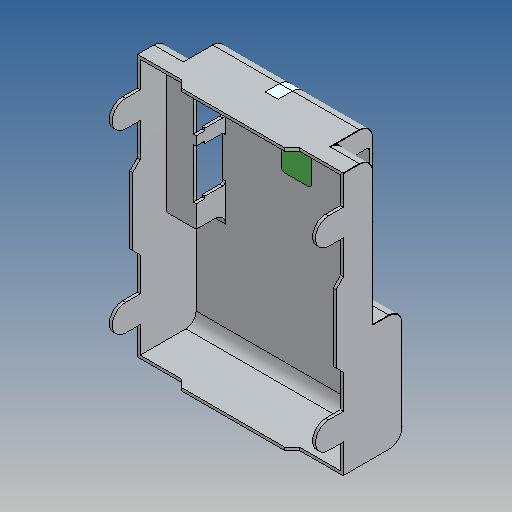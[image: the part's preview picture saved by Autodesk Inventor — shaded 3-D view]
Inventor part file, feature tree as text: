
AUTODESK INVENTOR PART (.ipt)
format: ipt  version: 2025 (Build 290162010, 162A)  size: 946,688 bytes
history: native  units: mm
features: sketch x4, extrude x3, fillet x2, direct_edit x1, delete_face x1, imported_body x1, revolve x1, move_body x1
ambient origin geometry x8: Origin, YZ Plane, XZ Plane, XY Plane, X Axis, Y Axis, Z Axis, Center Point
bodies: Volumenkörper1 (feature_tree), Volumenkörper2 (feature_tree), Volumenkörper3 (feature_tree)
feature tree (14):
  sketch  "Skizze1"  dims[d0=180.0deg d1=0.0mm d2=0.0mm d3=-0.58mm d4=10.0mm]
  direct_edit  "Direktbearbeitung1"
  delete_face  "Fläche löschen1"
  extrude  "Extrusion1"  TaperAngle=0.0deg  [1 undecoded]
  fillet  "Rundung2"  Radius=10.0mm
  extrude  "Extrusion2"  Depth=3.5mm TaperAngle=0.0deg
  extrude  "Extrusion3"  Depth=3.5mm TaperAngle=0.0deg
  fillet  "Rundung1"  Radius=0.1mm
  sketch  "Skizze2"  dims[d5=7.5mm d6=3.5mm d7=0.0mm]
  sketch  "Skizze3"  dims[d8=3.5mm d9=0.0mm d10=3.5mm d11=0.0mm d12=0.1mm]
  sketch  "Skizze4"  dims[d13=0.1mm]
  imported_body  "Basis1"
  revolve  "Drehen1"  [1 undecoded]
  move_body  "Verschieben1"
note: 2 required parameter values undecoded (feature->parameter linkage not recoverable at this tier; creation-order binding heuristic only, values carry confidence <= 0.55)
